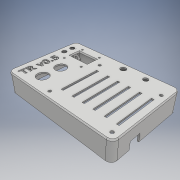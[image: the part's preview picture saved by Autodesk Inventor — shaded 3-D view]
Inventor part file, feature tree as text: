
AUTODESK INVENTOR PART (.ipt)
format: ipt  version: 2018.3 (Build 223284000, 284)  size: 505,344 bytes
history: native  units: mm
features: sketch x8, extrude x7, chamfer x7, emboss x1
ambient origin geometry x8: Origin, YZ Plane, XZ Plane, XY Plane, X Axis, Y Axis, Z Axis, Center Point
bodies: Solid1 (feature_tree)
feature tree (23):
  extrude  "Extrusion1"  Depth=101.6mm
  chamfer  "Chamfer1"  Distance=81.2mm
  chamfer  "Chamfer2"  Distance=8.0mm
  chamfer  "Chamfer3"  [1 undecoded]
  chamfer  "Chamfer4"  Distance=71.2mm
  chamfer  "Chamfer5"  Distance=4.0mm
  extrude  "Extrusion2"  Depth=8.0mm
  extrude  "Extrusion3"  Depth=0.5mm
  chamfer  "Chamfer6"  Distance=3.0mm
  extrude  "Extrusion4"  Depth=0.5mm
  extrude  "Extrusion5"  Depth=0.5mm
  extrude  "Extrusion6"  Depth=0.5mm
  chamfer  "Chamfer7"  Distance=29.464mm
  emboss  "Emboss1"
  extrude  "Extrusion8"  Depth=0.5mm
  sketch  "Sketch1"  dims[d0=152.4mm d1=101.6mm]
  sketch  "Sketch2"  dims[d2=7.0mm]
  sketch  "Sketch3"  dims[d3=6.86mm]
  sketch  "Sketch4"  dims[d4=10.0mm]
  sketch  "Sketch5"  dims[d5=35.0mm]
  sketch  "Sketch6"  dims[d6=4.0mm]
  sketch  "Sketch8"  dims[d7=4.0mm]
  sketch  "Sketch9"  dims[d8=4.0mm d9=81.2mm d10=8.0mm d11=0.0mm d12=71.2mm d13=4.0mm d14=8.0mm d15=3.0mm d16=3.0mm d17=28.956mm d18=22.0mm d19=3.0mm d20=29.464mm d21=3.0mm d22=16.0mm d23=16.0mm d24=20.0mm d25=63.2mm d26=36.0mm d27=36.0mm d28=25.0mm d29=10.0mm d30=0.0mm d31=8.0mm d32=8.0mm d33=6.0mm d34=12.0mm d35=8.0mm d36=8.1mm d37=10.0mm d38=65.0mm d39=0.0mm d40=28.956mm d41=15.0mm d42=9.398mm d43=0.0mm d44=3.0mm d45=51.0mm d46=10.2mm d47=3.0mm d48=51.0mm d49=3.0mm d50=51.0mm d51=3.0mm d52=51.0mm d53=3.0mm d54=51.0mm d55=3.0mm d56=51.0mm d57=21.36mm d58=35.33mm d59=49.3mm d60=63.2mm d61=80.24mm d62=2.0mm d63=0.0mm d64=1.0mm d65=2.0mm d66=45.0deg d67=1.0mm d68=2.0mm d69=45.0deg d70=1.0mm d71=2.0mm d72=45.0deg d73=1.0mm d74=2.0mm d75=45.0deg d76=1.0mm d77=2.0mm d78=45.0deg d79=2.0mm d80=25.0mm d81=0.0mm d82=8.0mm d83=14.0mm d84=0.0mm d85=8.0mm d86=2.0mm d87=45.0deg d88=3.5mm d89=7.0mm d90=7.0mm d91=3.5mm d92=7.0mm d93=7.0mm d94=3.5mm d95=7.0mm d96=7.0mm d97=3.5mm d98=7.0mm d99=7.0mm d100=12.0mm d101=0.0mm d102=11.0mm d103=14.0mm d105=0.0mm d106=10.0mm d107=0.0mm d108=0.0mm d109=0.0mm d110=10.0mm d111=0.0mm d112=8.0mm d113=0.0mm d116=0.2mm d117=2.0mm d118=45.0deg d119=1.5mm d120=0.0mm d122=7.0mm d123=7.0mm d124=0.5mm d125=0.0mm]
note: 1 required parameter value undecoded (feature->parameter linkage not recoverable at this tier; creation-order binding heuristic only, values carry confidence <= 0.55)
